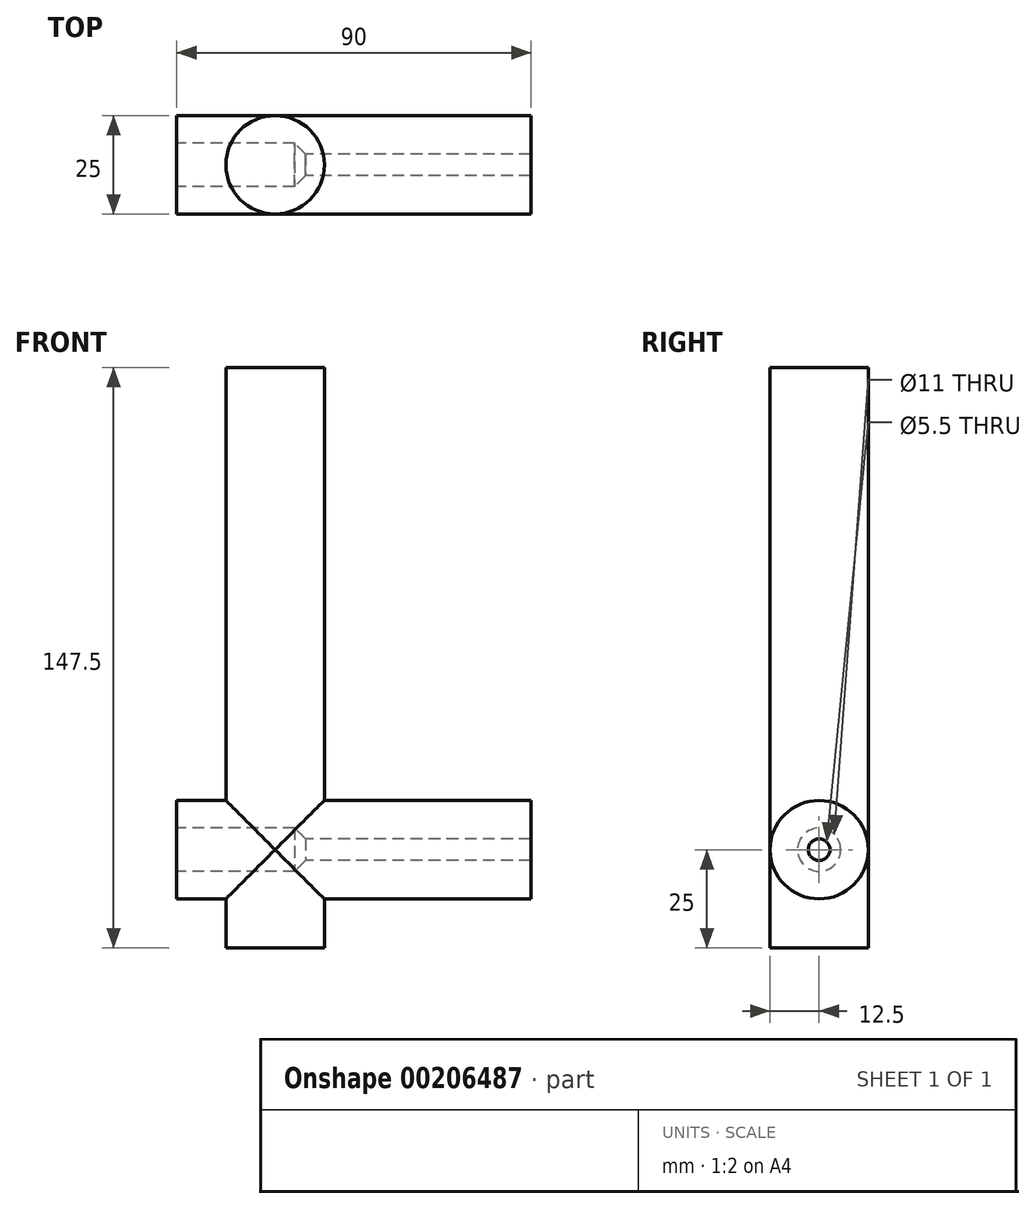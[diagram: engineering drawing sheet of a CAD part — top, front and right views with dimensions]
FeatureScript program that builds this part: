
annotation { "Feature Type Name" : "Feature", "Feature Type Description" : "" }
export const myFeature = defineFeature(function(context is Context, id is Id, definition is map)
    precondition{}
    {
        {
            var Q0;
            Q0=qCreatedBy(makeId("Top.planeOp"),FACE);
            var sketch = newSketch(context, id + "F0", { "sketchPlane" : qUnion([Q0])});
            skCircle(sketch, "E0", {"center": v(0, 0) * mm, "radius": 12.5 * mm});
            skSolve(sketch);
        }
        {
            var Q0;
            Q0=qSketchRegion(id+"F0",true);
            extrude(context, id + "F1", {"entities" : qUnion([Q0]), "depth" : 122.5 * mm, "offsetDistance" : 25 * mm});
        }
        {
            var Q0;
            Q0=qCreatedBy(makeId("Right.planeOp"),FACE);
            var sketch = newSketch(context, id + "F2", { "sketchPlane" : qUnion([Q0])});
            skCircle(sketch, "E1", {"center": v(0, 0) * mm, "radius": 12.5 * mm});
            skSolve(sketch);
        }
        {
            var Q0;
            Q0=qSketchRegion(id+"F2",true);
            extrude(context, id + "F3", {"entities" : qUnion([Q0]), "operationType" : NewBodyOperationType.ADD, "depth" : 65 * mm, "offsetDistance" : 25 * mm});
        }
        {
            var Q0;
            Q0=qSketchRegion(id+"F2",true);
            extrude(context, id + "F4", {"entities" : qUnion([Q0]), "operationType" : NewBodyOperationType.ADD, "oppositeDirection" : true, "depth" : 25 * mm, "offsetDistance" : 25 * mm});
        }
        {
            var Q0;
            Q0=qSketchRegion(id+"F0",true);
            extrude(context, id + "F5", {"entities" : qUnion([Q0]), "operationType" : NewBodyOperationType.ADD, "oppositeDirection" : true, "depth" : 25 * mm, "offsetDistance" : 25 * mm});
        }
        {
            var Q0;
            Q0=makeQuery(id+"F4.opExtrude","CAP_FACE",FACE,{"disambiguationData":[OSD([sQuery(id+"F2.wireOp",EDGE,"E1")])],"isStart":false});
            var sketch = newSketch(context, id + "F6", { "sketchPlane" : qUnion([Q0])});
            skPoint(sketch, "E2", {"position": v(0, 0) * mm});
            skCircle(sketch, "E3", {"center": v(0, 0) * mm, "radius": 5.5 * mm});
            skSolve(sketch);
        }
        {
            var Q0;
            Q0=makeQuery(id+"F6.imprint","IMPRINT",FACE,{"disambiguationData":[TD([[makeQuery(id+"F6.imprint","IMPRINT",EDGE,{"derivedFrom":sQuery(id+"F6.wireOp",EDGE,"E3")}),1.0]])]});
            extrude(context, id + "F7", {"entities" : qUnion([Q0]), "operationType" : NewBodyOperationType.REMOVE, "oppositeDirection" : true, "depth" : 30 * mm, "offsetDistance" : 25 * mm});
        }
        {
            var Q0;
            Q0=makeQuery(id+"F7.boolean.opBoolean","COPY",FACE,{"derivedFrom":makeQuery(id+"F7.opExtrude","CAP_FACE",FACE,{"disambiguationData":[OSD([sQuery(id+"F6.wireOp",EDGE,"E3")])],"isStart":false})});
            var sketch = newSketch(context, id + "F8", { "sketchPlane" : qUnion([Q0])});
            skPoint(sketch, "E4", {"position": v(0, 0) * mm});
            skSolve(sketch);
        }
        {
            var Q0;
            Q0=sQuery(id+"F8.wireOp",VERTEX,"E4");
            var Q1;
            Q1=makeQuery(id+"F1.opExtrude","SWEPT_BODY",BODY,{"disambiguationData":[OSD([sQuery(id+"F0.wireOp",EDGE,"E0")])]});
            hole(context, id + "F9", {"style" : HoleStyle.C_SINK, "endStyle" : HoleEndStyle.BLIND, "holeDiameter" : 5.5 * mm, "cSinkDiameter" : 11 * mm, "cSinkAngle" : 90 * degree, "majorDiameter" : 5 * mm, "holeDepth" : 100 * mm, "isTappedThrough" : true, "tappedDepth" : 12 * mm, "tapClearance" : 3, "locations" : qUnion([Q0]), "scope" : qUnion([Q1])});
        }
    });
